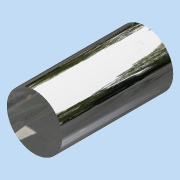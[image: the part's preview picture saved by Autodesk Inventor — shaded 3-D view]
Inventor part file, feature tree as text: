
AUTODESK INVENTOR PART (.ipt)
format: ipt  version: 2015 (Build 190159000, 159)  size: 93,184 bytes
history: native  units: in
note: dims shown in document units (in); Inventor stores cm internally (conversion verified against a paired STEP export)
features: extrude x1, sketch x1
ambient origin geometry x8: Origin, YZ Plane, XZ Plane, XY Plane, X Axis, Y Axis, Z Axis, Center Point
bodies: Solid1 (feature_tree)
feature tree (2):
  extrude  "Extrusion1"  Depth=0.5in TaperAngle=0.0deg
  sketch  "Sketch1"  dims[d0=0.25in d1=0.5in d2=0.0in]
